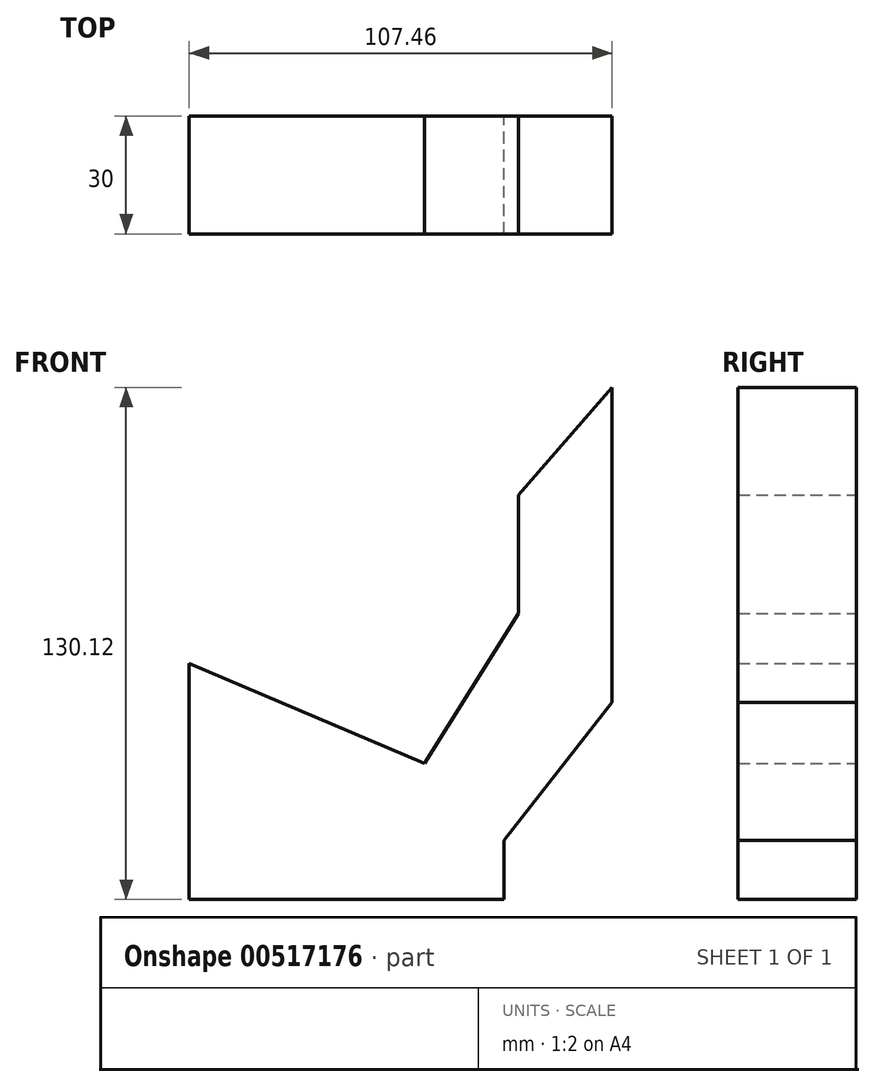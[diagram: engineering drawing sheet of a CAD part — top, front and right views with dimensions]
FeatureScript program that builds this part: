
annotation { "Feature Type Name" : "Feature", "Feature Type Description" : "" }
export const myFeature = defineFeature(function(context is Context, id is Id, definition is map)
    precondition{}
    {
        {
            var Q0;
            Q0=qCreatedBy(makeId("Front.planeOp"),FACE);
            var sketch = newSketch(context, id + "F0", { "sketchPlane" : qUnion([Q0])});
            skLineSegment(sketch, "E0", {"start": v(-118.2, 9.88) * mm, "end": v(-118.2, -50.12) * mm});
            skLineSegment(sketch, "E1", {"start": v(-118.2, -50.12) * mm, "end": v(-38.2, -50.12) * mm});
            skLineSegment(sketch, "E2", {"start": v(-38.2, -50.12) * mm, "end": v(-38.2, -35.12) * mm});
            skLineSegment(sketch, "E3", {"start": v(-38.2, -35.12) * mm, "end": v(-10.75, 0) * mm});
            skLineSegment(sketch, "E4", {"start": v(-10.75, 0) * mm, "end": v(-10.75, 80) * mm});
            skLineSegment(sketch, "E5", {"start": v(-10.75, 80) * mm, "end": v(-34.53, 52.64) * mm});
            skLineSegment(sketch, "E6", {"start": v(-34.53, 52.64) * mm, "end": v(-34.53, 22.64) * mm});
            skLineSegment(sketch, "E7", {"start": v(-34.53, 22.64) * mm, "end": v(-58.37, -15.52) * mm});
            skLineSegment(sketch, "E8", {"start": v(-58.37, -15.52) * mm, "end": v(-118.2, 9.88) * mm});
            skSolve(sketch);
        }
        {
            var Q0;
            Q0=makeQuery(id+"F0.imprint","IMPRINT",FACE,{"disambiguationData":[TD([[makeQuery(id+"F0.imprint","IMPRINT",EDGE,{"derivedFrom":sQuery(id+"F0.wireOp",EDGE,"E0")}),1.0]])]});
            extrude(context, id + "F1", {"entities" : qUnion([Q0]), "depth" : 30 * mm, "offsetDistance" : 25 * mm});
        }
    });
